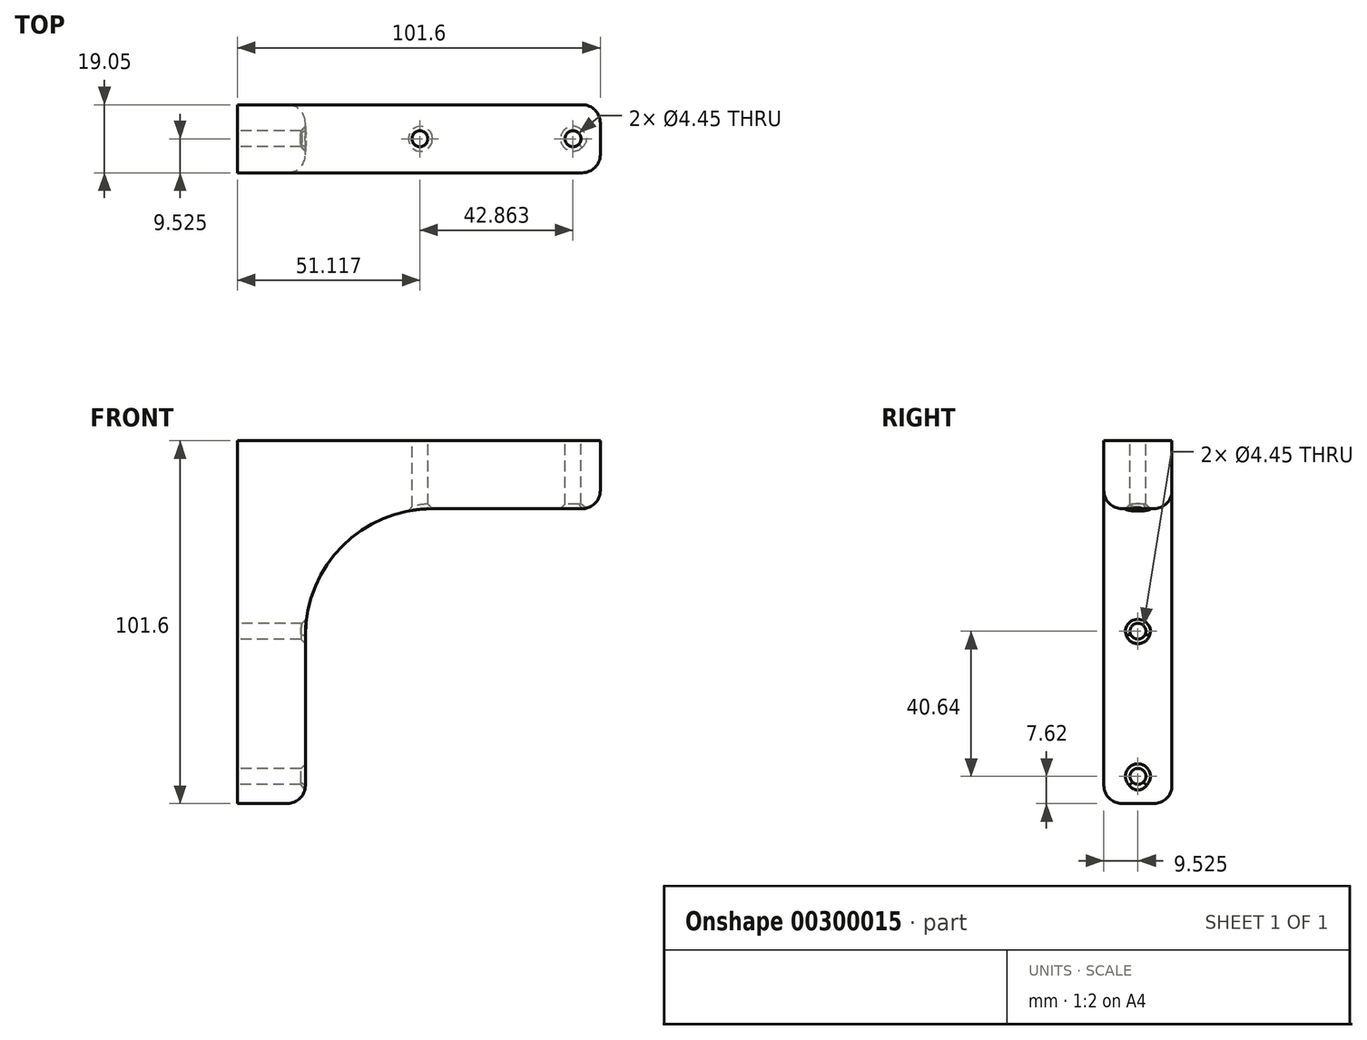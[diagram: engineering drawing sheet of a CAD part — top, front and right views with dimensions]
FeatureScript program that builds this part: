
annotation { "Feature Type Name" : "Feature", "Feature Type Description" : "" }
export const myFeature = defineFeature(function(context is Context, id is Id, definition is map)
    precondition{}
    {
        {
            var Q0;
            Q0=qCreatedBy(makeId("Front.planeOp"),FACE);
            var sketch = newSketch(context, id + "F0", { "sketchPlane" : qUnion([Q0])});
            skLineSegment(sketch, "E0", {"start": v(0, 0) * mm, "end": v(0, -101.6) * mm});
            skLineSegment(sketch, "E1", {"start": v(0, -101.6) * mm, "end": v(19.05, -101.6) * mm});
            skLineSegment(sketch, "E2", {"start": v(19.05, -101.6) * mm, "end": v(19.05, -19.05) * mm});
            skLineSegment(sketch, "E3", {"start": v(19.05, -19.05) * mm, "end": v(101.6, -19.05) * mm});
            skLineSegment(sketch, "E4", {"start": v(101.6, -19.05) * mm, "end": v(101.6, 0) * mm});
            skLineSegment(sketch, "E5", {"start": v(101.6, 0) * mm, "end": v(0, 0) * mm});
            skSolve(sketch);
        }
        {
            var Q0;
            Q0 = qSketchRegion(id + "F0", true);
            extrude(context, id + "F1", {"entities" : qUnion([Q0]), "depth" : 19.05 * mm});
        }
        {
            var Q0;
            Q0=makeQuery(id+"F1.opExtrude","SWEPT_EDGE",EDGE,{"disambiguationData":[OSD([sQuery(id+"F0.wireOp",EDGE,"E2"),sQuery(id+"F0.wireOp",EDGE,"E3")])]});
            fillet(context, id + "F2", {"entities" : qUnion([Q0]), "radius" : 35.56 * mm, "tangentPropagation" : true, "allowEdgeOverflow" : false});
        }
        {
            var Q0;
            Q0=makeQuery(id+"F1.opExtrude","SWEPT_EDGE",EDGE,{"disambiguationData":[OSD([sQuery(id+"F0.wireOp",EDGE,"E3"),sQuery(id+"F0.wireOp",EDGE,"E4")])]});
            var Q1;
            Q1=makeQuery(id+"F1.opExtrude","SWEPT_EDGE",EDGE,{"disambiguationData":[OSD([sQuery(id+"F0.wireOp",EDGE,"E1"),sQuery(id+"F0.wireOp",EDGE,"E2")])]});
            var Q2;
            {var subQ0=sQuery(id+"F0.wireOp",EDGE,"E3");var subQ1=sQuery(id+"F0.wireOp",EDGE,"E2");Q2=makeQuery(id+"F2.opFillet","BLEND_EDGE",EDGE,{"blendedFrom":[makeQuery(id+"F1.opExtrude","SWEPT_EDGE",EDGE,{"disambiguationData":[OSD([subQ1,subQ0])]}),makeQuery(id+"F1.opExtrude","CAP_FACE",FACE,{"disambiguationData":[OSD([sQuery(id+"F0.wireOp",EDGE,"E0"),sQuery(id+"F0.wireOp",EDGE,"E1"),subQ1,subQ0,sQuery(id+"F0.wireOp",EDGE,"E4"),sQuery(id+"F0.wireOp",EDGE,"E5")])],"isStart":false})],"blendedInto":[makeQuery(id+"F1.opExtrude","CAP_FACE",FACE,{"disambiguationData":[OSD([sQuery(id+"F0.wireOp",EDGE,"E0"),sQuery(id+"F0.wireOp",EDGE,"E1"),subQ1,subQ0,sQuery(id+"F0.wireOp",EDGE,"E4"),sQuery(id+"F0.wireOp",EDGE,"E5")])],"isStart":false})]});}
            var Q3;
            {var subQ0=sQuery(id+"F0.wireOp",EDGE,"E3");var subQ1=sQuery(id+"F0.wireOp",EDGE,"E2");Q3=makeQuery(id+"F2.opFillet","BLEND_EDGE",EDGE,{"blendedFrom":[makeQuery(id+"F1.opExtrude","SWEPT_EDGE",EDGE,{"disambiguationData":[OSD([subQ1,subQ0])]}),makeQuery(id+"F1.opExtrude","CAP_FACE",FACE,{"disambiguationData":[OSD([sQuery(id+"F0.wireOp",EDGE,"E0"),sQuery(id+"F0.wireOp",EDGE,"E1"),subQ1,subQ0,sQuery(id+"F0.wireOp",EDGE,"E4"),sQuery(id+"F0.wireOp",EDGE,"E5")])],"isStart":true})],"blendedInto":[makeQuery(id+"F1.opExtrude","CAP_FACE",FACE,{"disambiguationData":[OSD([sQuery(id+"F0.wireOp",EDGE,"E0"),sQuery(id+"F0.wireOp",EDGE,"E1"),subQ1,subQ0,sQuery(id+"F0.wireOp",EDGE,"E4"),sQuery(id+"F0.wireOp",EDGE,"E5")])],"isStart":true})]});}
            fillet(context, id + "F3", {"entities" : qUnion([Q0, Q1, Q2, Q3]), "radius" : 5.08 * mm, "tangentPropagation" : true, "allowEdgeOverflow" : false});
        }
        {
            var Q0;
            Q0=makeQuery(id+"F1.opExtrude","SWEPT_FACE",FACE,{"disambiguationData":[OSD([sQuery(id+"F0.wireOp",EDGE,"E0")])]});
            var sketch = newSketch(context, id + "F4", { "sketchPlane" : qUnion([Q0])});
            skCircle(sketch, "E6", {"center": v(9.53, -93.98) * mm, "radius": 2.22 * mm});
            skCircle(sketch, "E7", {"center": v(9.52, -53.34) * mm, "radius": 2.22 * mm});
            skSolve(sketch);
        }
        {
            var Q0;
            Q0=makeQuery(id+"F4.imprint","IMPRINT",FACE,{"disambiguationData":[TD([[makeQuery(id+"F4.imprint","IMPRINT",EDGE,{"derivedFrom":sQuery(id+"F4.wireOp",EDGE,"E7")}),1.0]])]});
            var Q1;
            Q1=makeQuery(id+"F4.imprint","IMPRINT",FACE,{"disambiguationData":[TD([[makeQuery(id+"F4.imprint","IMPRINT",EDGE,{"derivedFrom":sQuery(id+"F4.wireOp",EDGE,"E6")}),1.0]])]});
            extrude(context, id + "F5", {"entities" : qUnion([Q0, Q1]), "operationType" : NewBodyOperationType.REMOVE, "endBound" : BoundingType.THROUGH_ALL, "oppositeDirection" : true, "depth" : 25.4 * mm});
        }
        {
            var Q0;
            Q0=makeQuery(id+"F1.opExtrude","SWEPT_FACE",FACE,{"disambiguationData":[OSD([sQuery(id+"F0.wireOp",EDGE,"E5")])]});
            var sketch = newSketch(context, id + "F6", { "sketchPlane" : qUnion([Q0])});
            skCircle(sketch, "E8", {"center": v(93.98, -9.53) * mm, "radius": 2.22 * mm});
            skCircle(sketch, "E9", {"center": v(51.12, -9.53) * mm, "radius": 2.22 * mm});
            skSolve(sketch);
        }
        {
            var Q0;
            Q0=makeQuery(id+"F6.imprint","IMPRINT",FACE,{"disambiguationData":[TD([[makeQuery(id+"F6.imprint","IMPRINT",EDGE,{"derivedFrom":sQuery(id+"F6.wireOp",EDGE,"E8")}),1.0]])]});
            var Q1;
            Q1=makeQuery(id+"F6.imprint","IMPRINT",FACE,{"disambiguationData":[TD([[makeQuery(id+"F6.imprint","IMPRINT",EDGE,{"derivedFrom":sQuery(id+"F6.wireOp",EDGE,"E9")}),1.0]])]});
            extrude(context, id + "F7", {"entities" : qUnion([Q0, Q1]), "operationType" : NewBodyOperationType.REMOVE, "endBound" : BoundingType.THROUGH_ALL, "oppositeDirection" : true, "depth" : 25.4 * mm});
        }
        {
            var Q0;
            Q0=makeQuery(id+"F1.opExtrude","CAP_EDGE",EDGE,{"disambiguationData":[OSD([sQuery(id+"F0.wireOp",EDGE,"E1")])],"isStart":true});
            var Q1;
            Q1=makeQuery(id+"F1.opExtrude","CAP_EDGE",EDGE,{"disambiguationData":[OSD([sQuery(id+"F0.wireOp",EDGE,"E1")])],"isStart":false});
            var Q2;
            Q2=makeQuery(id+"F1.opExtrude","CAP_EDGE",EDGE,{"disambiguationData":[OSD([sQuery(id+"F0.wireOp",EDGE,"E4")])],"isStart":false});
            var Q3;
            Q3=makeQuery(id+"F1.opExtrude","CAP_EDGE",EDGE,{"disambiguationData":[OSD([sQuery(id+"F0.wireOp",EDGE,"E4")])],"isStart":true});
            fillet(context, id + "F8", {"entities" : qUnion([Q0, Q1, Q2, Q3]), "radius" : 5.08 * mm, "tangentPropagation" : true, "allowEdgeOverflow" : false});
        }
        {
            var Q0;
            Q0=makeQuery(id+"F7.boolean.opBoolean","INTERSECT",EDGE,{"derivedFrom":[makeQuery(id+"F2.opFillet","BLEND_FACE",FACE,{"disambiguationData":[OSD([sQuery(id+"F0.wireOp",EDGE,"E2"),sQuery(id+"F0.wireOp",EDGE,"E3")])]}),makeQuery(id+"F7.opExtrude","SWEPT_FACE",FACE,{"disambiguationData":[OSD([sQuery(id+"F6.wireOp",EDGE,"E9")])]})]});
            var Q1;
            Q1=makeQuery(id+"F7.boolean.opBoolean","INTERSECT",EDGE,{"derivedFrom":[makeQuery(id+"F1.opExtrude","SWEPT_FACE",FACE,{"disambiguationData":[OSD([sQuery(id+"F0.wireOp",EDGE,"E3")])]}),makeQuery(id+"F7.opExtrude","SWEPT_FACE",FACE,{"disambiguationData":[OSD([sQuery(id+"F6.wireOp",EDGE,"E8")])]})]});
            var Q2;
            Q2=makeQuery(id+"F5.boolean.opBoolean","INTERSECT",EDGE,{"derivedFrom":[makeQuery(id+"F2.opFillet","BLEND_FACE",FACE,{"disambiguationData":[OSD([sQuery(id+"F0.wireOp",EDGE,"E2"),sQuery(id+"F0.wireOp",EDGE,"E3")])]}),makeQuery(id+"F5.opExtrude","SWEPT_FACE",FACE,{"disambiguationData":[OSD([sQuery(id+"F4.wireOp",EDGE,"E7")])]})]});
            var Q3;
            Q3=makeQuery(id+"F5.boolean.opBoolean","INTERSECT",EDGE,{"derivedFrom":[makeQuery(id+"F1.opExtrude","SWEPT_FACE",FACE,{"disambiguationData":[OSD([sQuery(id+"F0.wireOp",EDGE,"E2")])]}),makeQuery(id+"F5.opExtrude","SWEPT_FACE",FACE,{"disambiguationData":[OSD([sQuery(id+"F4.wireOp",EDGE,"E6")])]})]});
            chamfer(context, id + "F9", {"entities" : qUnion([Q0, Q1, Q2, Q3]), "width" : 1.27 * mm, "tangentPropagation" : true});
        }
    });
